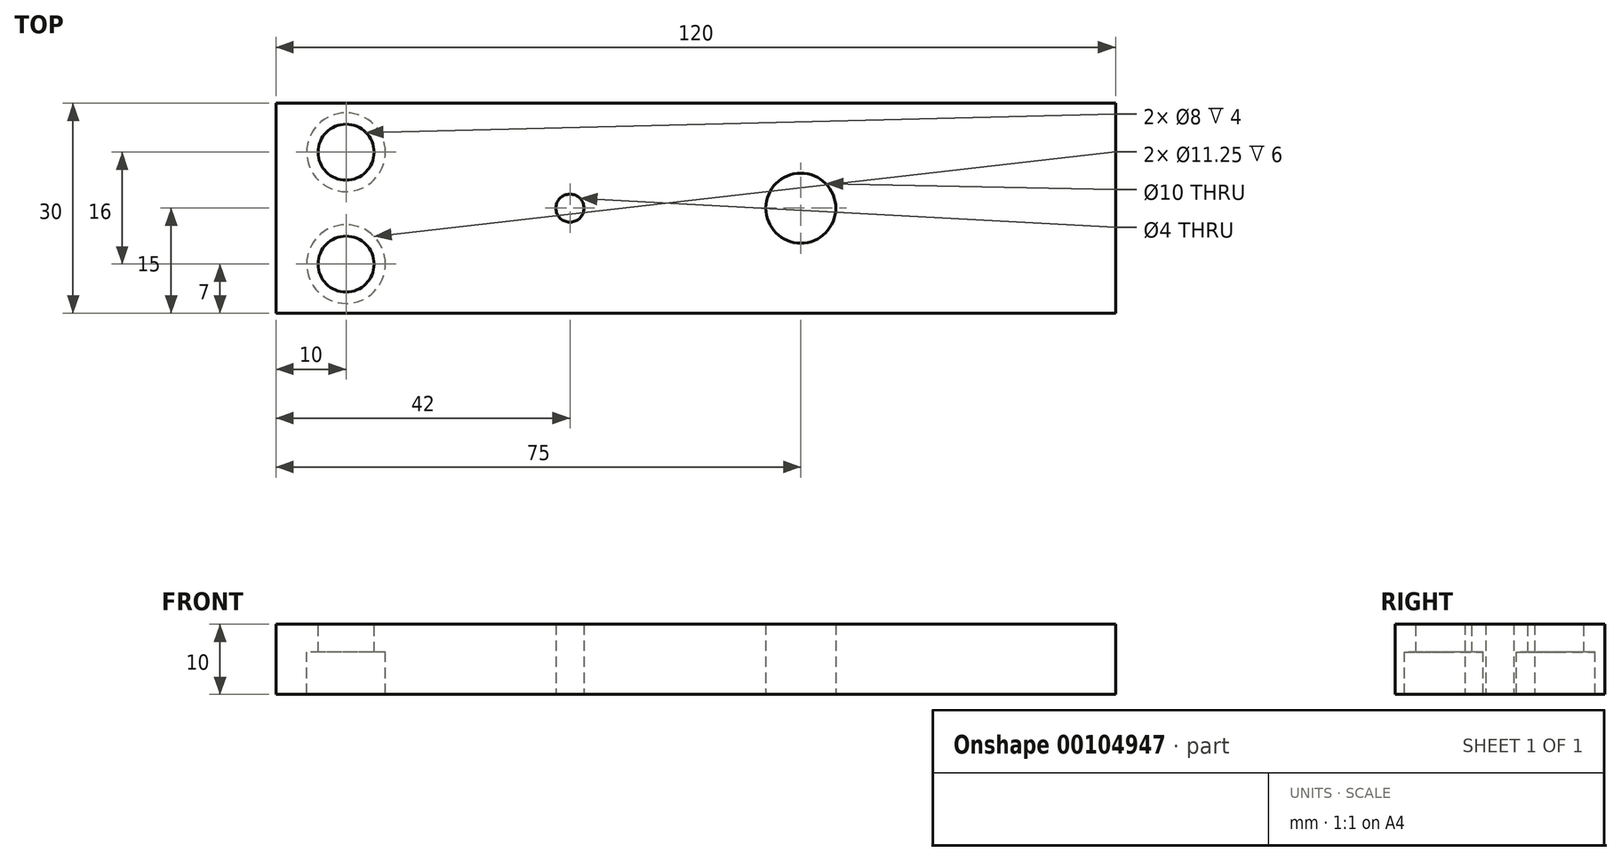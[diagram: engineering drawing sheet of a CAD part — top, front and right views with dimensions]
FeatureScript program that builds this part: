
annotation { "Feature Type Name" : "Feature", "Feature Type Description" : "" }
export const myFeature = defineFeature(function(context is Context, id is Id, definition is map)
    precondition{}
    {
        {
            var Q0;
            Q0=qCreatedBy(makeId("Top.planeOp"),FACE);
            var sketch = newSketch(context, id + "F0", { "sketchPlane" : qUnion([Q0])});
            skCircle(sketch, "E0", {"center": v(0, 0) * mm, "radius": 5 * mm});
            skLineSegment(sketch, "E1.bottom", {"start": v(45, 15) * mm, "end": v(-75, 15) * mm});
            skLineSegment(sketch, "E1.top", {"start": v(45, -15) * mm, "end": v(-75, -15) * mm});
            skLineSegment(sketch, "E1.left", {"start": v(45, 15) * mm, "end": v(45, -15) * mm});
            skLineSegment(sketch, "E1.right", {"start": v(-75, 15) * mm, "end": v(-75, -15) * mm});
            skSolve(sketch);
        }
        {
            var Q0;
            Q0 = qSketchRegion(id + "F0", true);
            extrude(context, id + "F1", {"entities" : qUnion([Q0]), "depth" : 10 * mm});
        }
        {
            var Q0;
            Q0=makeQuery(id+"F1.opExtrude","CAP_FACE",FACE,{"disambiguationData":[OSD([sQuery(id+"F0.wireOp",EDGE,"E0"),sQuery(id+"F0.wireOp",EDGE,"E1.bottom"),sQuery(id+"F0.wireOp",EDGE,"E1.top"),sQuery(id+"F0.wireOp",EDGE,"E1.left"),sQuery(id+"F0.wireOp",EDGE,"E1.right")])],"isStart":true});
            var sketch = newSketch(context, id + "F2", { "sketchPlane" : qUnion([Q0])});
            skPoint(sketch, "E2", {"position": v(-65, 8) * mm});
            skPoint(sketch, "E3", {"position": v(-65, -8) * mm});
            skSolve(sketch);
        }
        {
            var Q0;
            Q0=sQuery(id+"F2.wireOp",VERTEX,"E2");
            var Q1;
            Q1=sQuery(id+"F2.wireOp",VERTEX,"E3");
            var Q2;
            Q2=makeQuery(id+"F1.opExtrude","SWEPT_BODY",BODY,{"disambiguationData":[OSD([sQuery(id+"F0.wireOp",EDGE,"E0"),sQuery(id+"F0.wireOp",EDGE,"E1.bottom"),sQuery(id+"F0.wireOp",EDGE,"E1.top"),sQuery(id+"F0.wireOp",EDGE,"E1.left"),sQuery(id+"F0.wireOp",EDGE,"E1.right")])]});
            hole(context, id + "F3", {"style" : HoleStyle.C_BORE, "endStyle" : HoleEndStyle.THROUGH, "standardTappedOrClearance" : lookupTablePath({ "standard" : "ISO", "size" : "8", "type" : "Drilled" }), "standardBlindInLast" : lookupTablePath({ "standard" : "ISO", "size" : "8", "type" : "Drilled" }), "holeDiameter" : 8 * mm, "cBoreDiameter" : 11.25 * mm, "cBoreDepth" : 6 * mm, "startFromSketch" : true, "locations" : qUnion([Q0, Q1]), "scope" : qUnion([Q2]), "isTappedThrough" : true});
        }
        {
            var Q0;
            Q0=makeQuery(id+"F1.opExtrude","CAP_FACE",FACE,{"disambiguationData":[OSD([sQuery(id+"F0.wireOp",EDGE,"E0"),sQuery(id+"F0.wireOp",EDGE,"E1.bottom"),sQuery(id+"F0.wireOp",EDGE,"E1.top"),sQuery(id+"F0.wireOp",EDGE,"E1.left"),sQuery(id+"F0.wireOp",EDGE,"E1.right")])],"isStart":false});
            var sketch = newSketch(context, id + "F4", { "sketchPlane" : qUnion([Q0])});
            skPoint(sketch, "E4", {"position": v(-33, 0) * mm});
            skSolve(sketch);
        }
        {
            var Q0;
            Q0=sQuery(id+"F4.wireOp",VERTEX,"E4");
            var Q1;
            Q1=makeQuery(id+"F1.opExtrude","SWEPT_BODY",BODY,{"disambiguationData":[OSD([sQuery(id+"F0.wireOp",EDGE,"E0"),sQuery(id+"F0.wireOp",EDGE,"E1.bottom"),sQuery(id+"F0.wireOp",EDGE,"E1.top"),sQuery(id+"F0.wireOp",EDGE,"E1.left"),sQuery(id+"F0.wireOp",EDGE,"E1.right")])]});
            hole(context, id + "F5", {"style" : HoleStyle.SIMPLE, "endStyle" : HoleEndStyle.THROUGH, "standardTappedOrClearance" : lookupTablePath({ "standard" : "ISO", "size" : "4", "type" : "Drilled" }), "standardBlindInLast" : lookupTablePath({ "standard" : "ISO", "size" : "4", "type" : "Drilled" }), "holeDiameter" : 4 * mm, "startFromSketch" : true, "locations" : qUnion([Q0]), "scope" : qUnion([Q1]), "isTappedThrough" : true});
        }
    });
